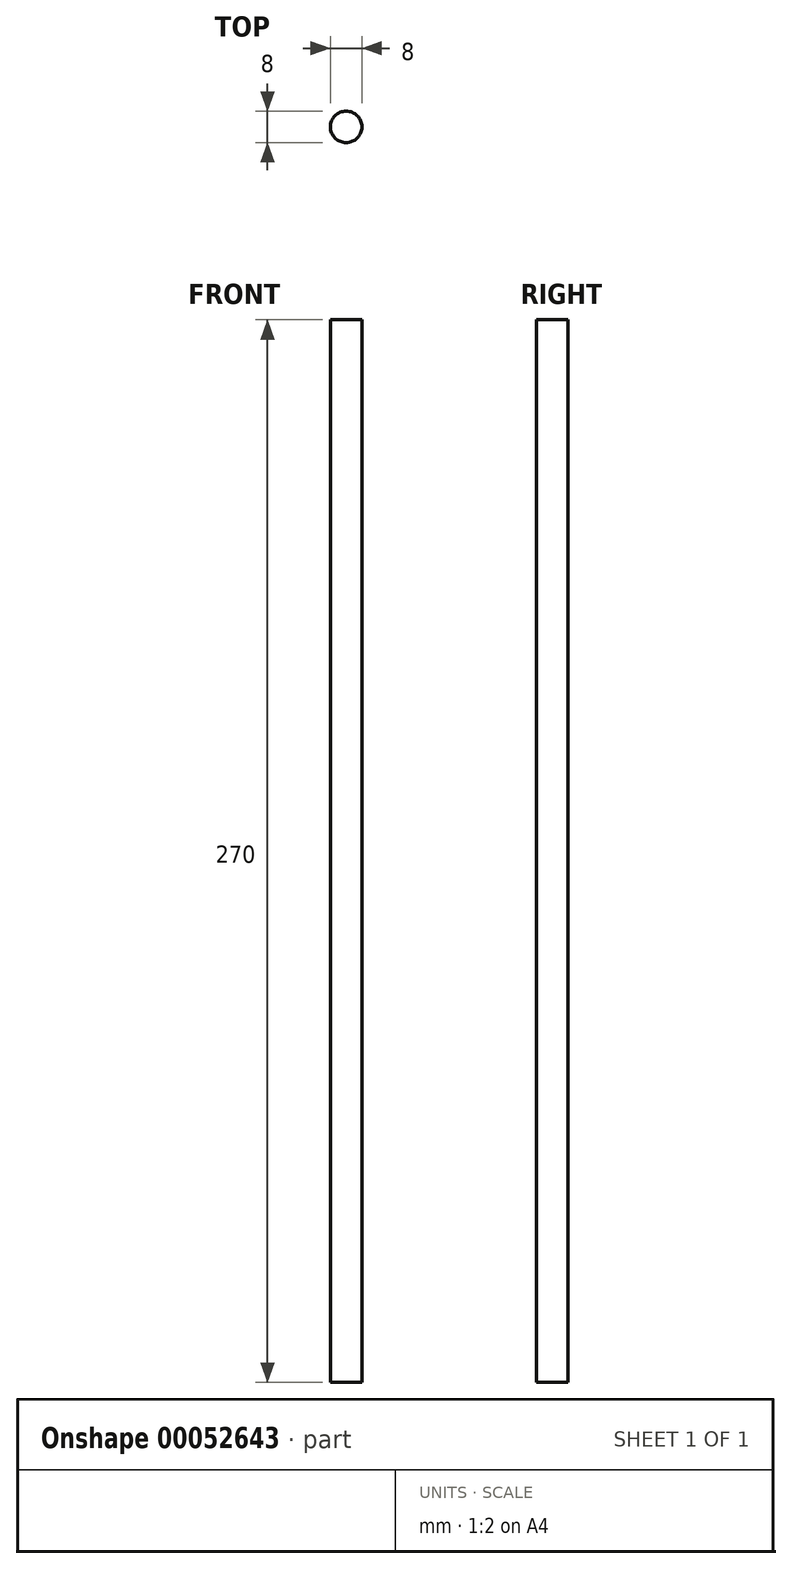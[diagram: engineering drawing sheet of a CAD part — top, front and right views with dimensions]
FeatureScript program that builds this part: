
annotation { "Feature Type Name" : "Feature", "Feature Type Description" : "" }
export const myFeature = defineFeature(function(context is Context, id is Id, definition is map)
    precondition{}
    {
        {
            var Q0;
            Q0=qCreatedBy(makeId("Top.planeOp"),FACE);
            var sketch = newSketch(context, id + "F0", { "sketchPlane" : qUnion([Q0])});
            skCircle(sketch, "E0", {"center": v(0, 0) * mm, "radius": 4 * mm});
            skSolve(sketch);
        }
        {
            var Q0;
            Q0=qSketchRegion(id+"F0",true);
            extrude(context, id + "F1", {"entities" : qUnion([Q0]), "depth" : 270 * mm});
        }
    });
